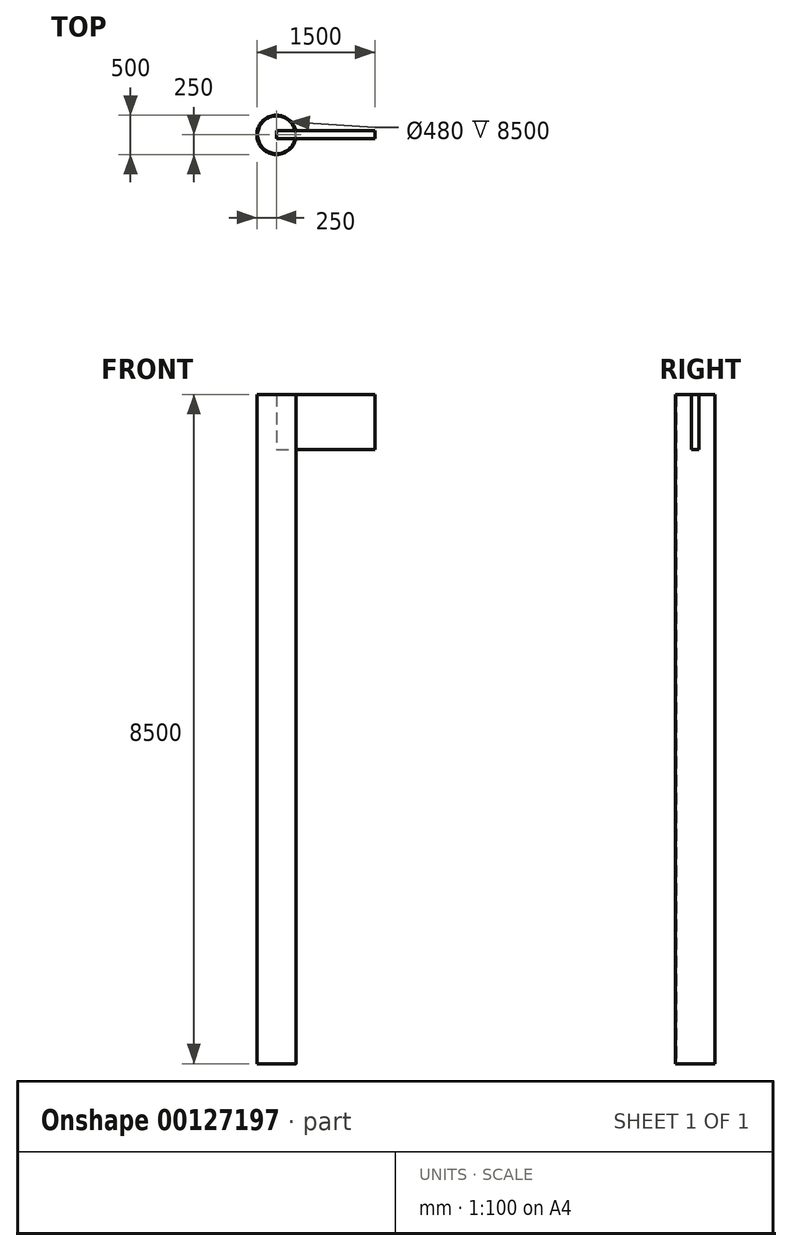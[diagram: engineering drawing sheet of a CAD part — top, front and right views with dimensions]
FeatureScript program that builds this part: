
annotation { "Feature Type Name" : "Feature", "Feature Type Description" : "" }
export const myFeature = defineFeature(function(context is Context, id is Id, definition is map)
    precondition{}
    {
        {
            var Q0;
            Q0=qCreatedBy(makeId("Top.planeOp"),FACE);
            var sketch = newSketch(context, id + "F0", { "sketchPlane" : qUnion([Q0])});
            skCircle(sketch, "E0", {"center": v(0, 0) * mm, "radius": 250 * mm});
            skCircle(sketch, "E1.0", {"center": v(0, 0) * mm, "radius": 240 * mm});
            skSolve(sketch);
        }
        {
            var Q0;
            Q0=makeQuery(id+"F0.imprint","IMPRINT",FACE,{"disambiguationData":[TD([[makeQuery(id+"F0.imprint","IMPRINT",EDGE,{"derivedFrom":sQuery(id+"F0.wireOp",EDGE,"E0")}),1.0]])]});
            extrude(context, id + "F1", {"entities" : qUnion([Q0]), "depth" : 8500 * mm});
        }
        {
            var Q0;
            Q0=qCreatedBy(makeId("Front.planeOp"),FACE);
            var sketch = newSketch(context, id + "F2", { "sketchPlane" : qUnion([Q0])});
            skLineSegment(sketch, "E2.bottom", {"start": v(0, 8500) * mm, "end": v(1250, 8500) * mm});
            skLineSegment(sketch, "E2.top", {"start": v(0, 7800) * mm, "end": v(1250, 7800) * mm});
            skLineSegment(sketch, "E2.left", {"start": v(0, 8500) * mm, "end": v(0, 7800) * mm});
            skLineSegment(sketch, "E2.right", {"start": v(1250, 8500) * mm, "end": v(1250, 7800) * mm});
            skSolve(sketch);
        }
        {
            var Q0;
            Q0=makeQuery(id+"F2.imprint","IMPRINT",FACE,{"disambiguationData":[TD([[makeQuery(id+"F2.imprint","IMPRINT",EDGE,{"derivedFrom":sQuery(id+"F2.wireOp",EDGE,"E2.bottom")}),-1.0]])]});
            extrude(context, id + "F3", {"entities" : qUnion([Q0]), "operationType" : NewBodyOperationType.ADD, "depth" : 50 * mm, "hasSecondDirection" : true, "secondDirectionOppositeDirection" : true, "secondDirectionDepth" : 50 * mm});
        }
    });
